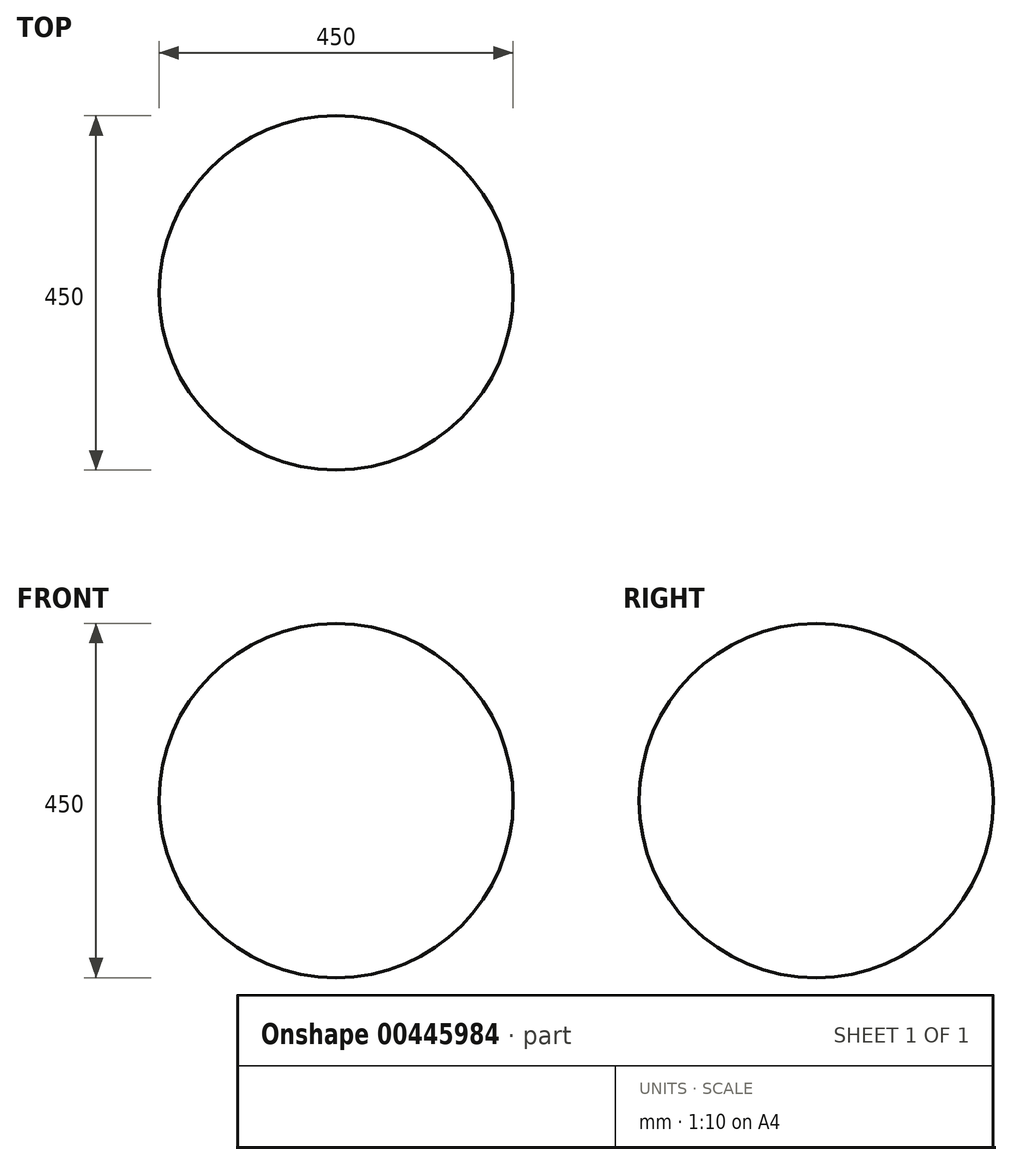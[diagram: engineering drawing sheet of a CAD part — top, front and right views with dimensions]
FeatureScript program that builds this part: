
annotation { "Feature Type Name" : "Feature", "Feature Type Description" : "" }
export const myFeature = defineFeature(function(context is Context, id is Id, definition is map)
    precondition{}
    {
        {
            var Q0;
            Q0=qCreatedBy(makeId("Top.planeOp"),FACE);
            var sketch = newSketch(context, id + "F0", { "sketchPlane" : qUnion([Q0])});
            skArc(sketch, "E0", {"start": v(0, -225) * mm, "mid": v(225, 0) * mm, "end": v(0, 225) * mm});
            skLineSegment(sketch, "E1", {"start": v(0, 225) * mm, "end": v(0, -225) * mm});
            skSolve(sketch);
        }
        {
            var Q0;
            Q0=makeQuery(id+"F0.imprint","IMPRINT",FACE,{"disambiguationData":[TD([[makeQuery(id+"F0.imprint","IMPRINT",EDGE,{"derivedFrom":sQuery(id+"F0.wireOp",EDGE,"E0")}),1.0]])]});
            var Q1;
            Q1=sQuery(id+"F0.wireOp",EDGE,"E1");
            revolve(context, id + "F1", {"entities" : qUnion([Q0]), "axis" : qUnion([Q1]), "revolveType" : RevolveType.FULL});
        }
    });
